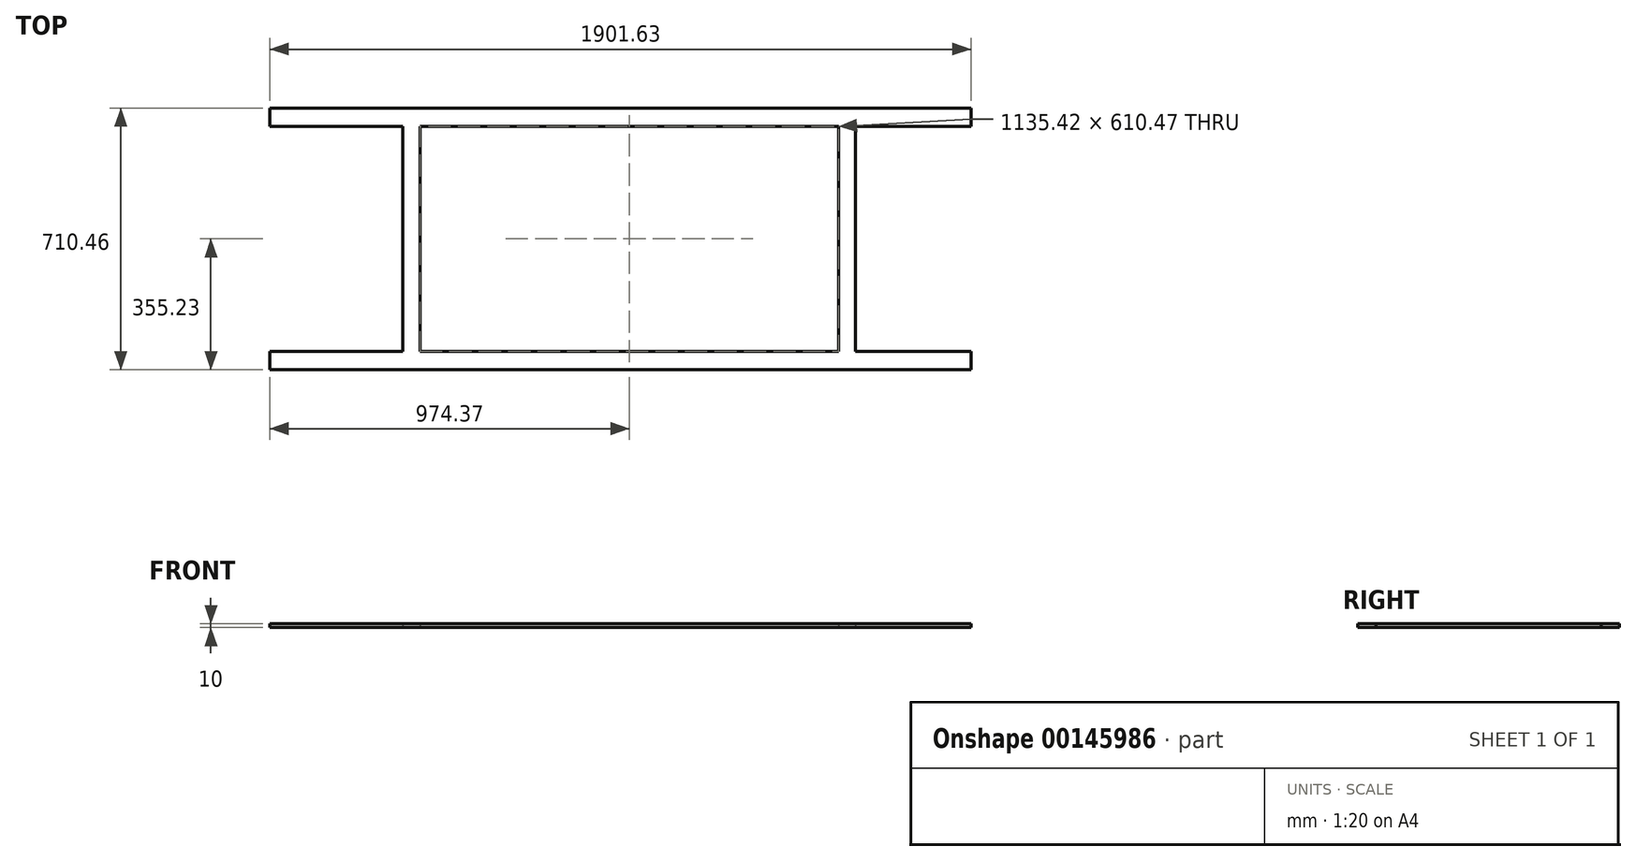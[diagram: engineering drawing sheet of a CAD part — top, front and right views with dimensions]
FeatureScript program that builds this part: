
annotation { "Feature Type Name" : "Feature", "Feature Type Description" : "" }
export const myFeature = defineFeature(function(context is Context, id is Id, definition is map)
    precondition{}
    {
        {
            var Q0;
            Q0=qCreatedBy(makeId("Top.planeOp"),FACE);
            var sketch = newSketch(context, id + "F0", { "sketchPlane" : qUnion([Q0])});
            skLineSegment(sketch, "E0.bottom", {"start": v(-614.3, 355.23) * mm, "end": v(614.3, 355.23) * mm});
            skLineSegment(sketch, "E0.top", {"start": v(-614.3, -355.23) * mm, "end": v(614.3, -355.23) * mm});
            skLineSegment(sketch, "E0.left", {"start": v(-614.3, 305.23) * mm, "end": v(-614.3, -305.23) * mm});
            skLineSegment(sketch, "E0.right", {"start": v(614.3, 305.23) * mm, "end": v(614.3, -305.23) * mm});
            skPoint(sketch, "E0.middle", {"position": v(0, 0) * mm});
            skLineSegment(sketch, "E1.bottom", {"start": v(-567.71, 305.23) * mm, "end": v(567.71, 305.23) * mm});
            skLineSegment(sketch, "E1.top", {"start": v(-567.71, -305.23) * mm, "end": v(567.71, -305.23) * mm});
            skLineSegment(sketch, "E1.left", {"start": v(-567.71, 305.23) * mm, "end": v(-567.71, -305.23) * mm});
            skLineSegment(sketch, "E1.right", {"start": v(567.71, 305.23) * mm, "end": v(567.71, -305.23) * mm});
            skLineSegment(sketch, "E2", {"start": v(-614.3, 355.23) * mm, "end": v(-974.37, 355.23) * mm});
            skLineSegment(sketch, "E3", {"start": v(-974.37, 355.23) * mm, "end": v(-974.37, 305.23) * mm});
            skLineSegment(sketch, "E4", {"start": v(-974.37, 305.23) * mm, "end": v(-974.37, 355.23) * mm});
            skLineSegment(sketch, "E5", {"start": v(-974.37, 305.23) * mm, "end": v(-614.3, 305.23) * mm});
            skLineSegment(sketch, "E6", {"start": v(614.3, 355.23) * mm, "end": v(927.26, 355.23) * mm});
            skLineSegment(sketch, "E7", {"start": v(927.26, 355.23) * mm, "end": v(927.26, 305.23) * mm});
            skLineSegment(sketch, "E8", {"start": v(927.26, 305.23) * mm, "end": v(614.3, 305.23) * mm});
            skLineSegment(sketch, "E9", {"start": v(-614.3, -355.23) * mm, "end": v(-974.37, -355.23) * mm});
            skLineSegment(sketch, "E10", {"start": v(-614.3, -305.23) * mm, "end": v(-974.37, -305.23) * mm});
            skLineSegment(sketch, "E11", {"start": v(-974.37, -305.23) * mm, "end": v(-974.37, -355.23) * mm});
            skLineSegment(sketch, "E12", {"start": v(614.3, -355.23) * mm, "end": v(927.26, -355.23) * mm});
            skLineSegment(sketch, "E13", {"start": v(927.26, -355.23) * mm, "end": v(927.26, -305.23) * mm});
            skLineSegment(sketch, "E14", {"start": v(927.26, -305.23) * mm, "end": v(614.3, -305.23) * mm});
            skSolve(sketch);
        }
        {
            var Q0;
            Q0=makeQuery(id+"F0.imprint","IMPRINT",FACE,{"disambiguationData":[TD([[makeQuery(id+"F0.imprint","IMPRINT",EDGE,{"derivedFrom":sQuery(id+"F0.wireOp",EDGE,"E0.bottom")}),-1.0]])]});
            extrude(context, id + "F1", {"entities" : qUnion([Q0]), "depth" : 10 * mm});
        }
    });
